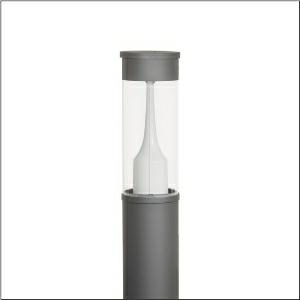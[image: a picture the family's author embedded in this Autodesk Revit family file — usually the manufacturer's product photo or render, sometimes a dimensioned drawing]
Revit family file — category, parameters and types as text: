
# Revit family: city-light_260_iq___st1_2a_5xa5295mf14h_84f0
name_source: partatom
category: Lighting Fixtures
units: mm (PartAtom-declared; Revit-internal decimal feet)

## family parameters
Cut with Voids When Loaded = No
Host = Face
Light Source = No
Part Type = Normal
Room Calculation Point = No
Round Connector Dimension = Use Diameter
Shared = No

## types (1)
- --- (1 x LED, 1540 lm, 11.8 W, 2700K)
    Apparent Load = 12 VA
    CIE Flux Codes = 22 61 93 96 100
    Color Rendering = 70
    Color Temperature = 2700K
    Default Elevation = 1800 mm
    Description = City-Light 260 iQ, light pillar, Module 540 iQ-SR, primary light control with 3 zone facetted reflector, of plastic, silver coated, highly specular, structured, primary optical cover: cover, of PMMA, transparent, partly coated, light distribution: ST1.2a, primary light characteristic: asymmetric, LED, High Power LED, rated luminous flux: 1.540lm, luminous efficacy: 131lm/W, light colour: 727, colour temperature: 2700K, control gear: iQ Street-Remote, control: pre-setting: logarithmic dimming characteristic, Street-Remote, Auto-Match, Temp-Guard, Lumen-Switch, Night-Set, Smart-Wire, Light-Fading, Desk-Remote (wireless, voltage-free reading and setting of iQ features in the workshop via application-optimized NFC function/RFID function), optimised constant luminous flux control (CLO 2.0), with terminal, 6-pole, max. 2.5mm², mains connection: 230..240V, AC, 50/60Hz, start of lifetime: 12W, end of service life: 12W, reduction: 6W, luminaire housing, cylindrical, of extruded aluminium section, coated, Siteco® metallic grey (DB 702S), length: 2.600mm, diameter: 200mm, Module 540 iQ-SR, traffic white (RAL 9016), equipment: standard, protection rating (complete): IP65, insulation class (complete): insulation class II (safety insulation), certification: CE, ENEC, VDE, packaging unit: 1 piece

Light Distribution: ST1.2a
    Height = 500 mm
    Lamp = 1 x LED
    Lamp Light Flux = 1540 lm
    Lamp Power = 11.8 W
    Lamp count = 1
    Length = 200 mm  [stored 0.656168 ft]
    Luminous efficacy = 131 lm/W
    Manufacturer = Siteco
    ModVariant = No
    Model = 5XA5295MF14H
    Mounting Place = Floor
    Mounting Type = Freestanding
    Number of Poles = 1
    OnlyDefault = Yes
    Power Factor = 1
    Product Name = City-Light 260 iQ | ST1.2a
    Product group = light pillar
    ProductGroupID = 1301
    Protection Class = Protection class II
    Protection Degree = IP 65
    RLX_Detail_Level = 1
    RLX_Emergency_Light_Flux = 0 lm
    RLX_Emergency_Type = 0
    RLX_Emergency_Type_DB = No
    RlxData = <blob elided: 53781 chars, md5=b219eef7>
    Socket = socket
    Standby Power = 0 W
    System Light Flux = 1540 lm
    System Power = 12 W
    Type Comments = factory setting: luminous flux: 100 % | dim-lin: 254 | 472 mA
    Type Image = l_1006918.jpg
    URL = http://relux.com
    VarID = @adj_153126
    Voltage = 0 V
    Weight = 0.00 kg
    Width = 0 mm  [stored 0 ft]

note: [stored X ft] marks values corroborated as IEEE doubles in the binary element streams (Revit-internal decimal feet)

## geometry (parser evidence)
native form markers: Blend x4, Sweep x13
no freeform markers — native parametric forms only
